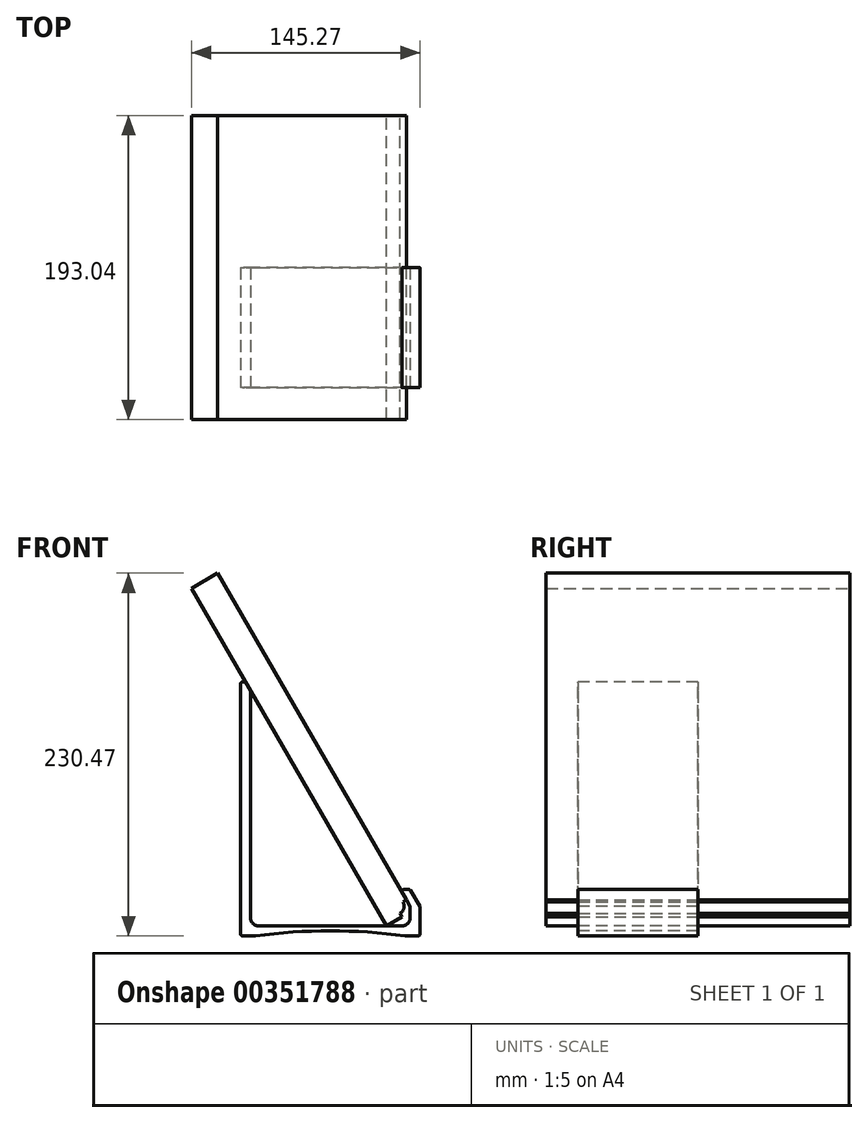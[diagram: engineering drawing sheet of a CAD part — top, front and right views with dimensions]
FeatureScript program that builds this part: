
annotation { "Feature Type Name" : "Feature", "Feature Type Description" : "" }
export const myFeature = defineFeature(function(context is Context, id is Id, definition is map)
    precondition{}
    {
        {
            var Q0;
            Q0=qCreatedBy(makeId("Front.planeOp"),FACE);
            var sketch = newSketch(context, id + "F0", { "sketchPlane" : qUnion([Q0])});
            skLineSegment(sketch, "E0", {"start": v(0, 0) * mm, "end": v(0, 247.65) * mm});
            skLineSegment(sketch, "E1", {"start": v(0, 247.65) * mm, "end": v(19.3, 247.65) * mm});
            skLineSegment(sketch, "E2", {"start": v(19.3, 247.65) * mm, "end": v(19.3, 7.87) * mm});
            skLineSegment(sketch, "E3", {"start": v(19.3, 7.87) * mm, "end": v(16.76, 7.87) * mm});
            skLineSegment(sketch, "E4", {"start": v(11.43, 2.54) * mm, "end": v(11.43, 0) * mm});
            skLineSegment(sketch, "E5", {"start": v(11.43, 0) * mm, "end": v(0, 0) * mm});
            skArc(sketch, "E6", {"start": v(11.43, 2.54) * mm, "mid": v(15.2, 4.1) * mm, "end": v(16.76, 7.87) * mm});
            skSolve(sketch);
        }
        {
            var Q0;
            Q0 = qSketchRegion(id + "F0", true);
            extrude(context, id + "F1", {"entities" : qUnion([Q0]), "endBound" : BoundingType.SYMMETRIC, "depth" : 193.04 * mm});
        }
        {
            var Q0;
            Q0=makeQuery(id+"F1.opExtrude","SWEPT_BODY",BODY,{"disambiguationData":[OSD([sQuery(id+"F0.wireOp",EDGE,"E0"),sQuery(id+"F0.wireOp",EDGE,"E1"),sQuery(id+"F0.wireOp",EDGE,"E2"),sQuery(id+"F0.wireOp",EDGE,"E3"),sQuery(id+"F0.wireOp",EDGE,"E4"),sQuery(id+"F0.wireOp",EDGE,"E5"),sQuery(id+"F0.wireOp",EDGE,"E6")])]});
            var Q1;
            Q1=makeQuery(id+"F1.opExtrude","SWEPT_EDGE",EDGE,{"disambiguationData":[OSD([sQuery(id+"F0.wireOp",EDGE,"E0"),sQuery(id+"F0.wireOp",EDGE,"E5")])]});
            transform(context, id + "F2", {"entities" : qUnion([Q0]), "transformType" : TransformType.ROTATION, "transformAxis" : qUnion([Q1]), "angle" : 30 * degree, "oppositeDirection" : true, "makeCopy" : false});
        }
        {
            var Q0;
            Q0=qCreatedBy(makeId("Front.planeOp"),FACE);
            cPlane(context, id + "F3", {"entities" : qUnion([Q0]), "cplaneType" : CPlaneType.OFFSET, "offset" : 76.2 * mm, "width" : 152.4 * mm, "height" : 152.4 * mm});
        }
        {
            var Q0;
            Q0=qCreatedBy(id+"F3.planeOp",FACE);
            var sketch = newSketch(context, id + "F4", { "sketchPlane" : qUnion([Q0])});
            skLineSegment(sketch, "E7", {"start": v(15.07, 23.07) * mm, "end": v(21.44, 12.03) * mm});
            skLineSegment(sketch, "E8", {"start": v(21.44, 12.03) * mm, "end": v(21.44, -6.35) * mm});
            skLineSegment(sketch, "E9", {"start": v(21.44, -6.35) * mm, "end": v(11.92, -6.35) * mm});
            skLineSegment(sketch, "E10", {"start": v(-92.66, -6.35) * mm, "end": v(-92.66, 155) * mm});
            skLineSegment(sketch, "E11", {"start": v(-92.66, 155) * mm, "end": v(-89.49, 155) * mm});
            skLineSegment(sketch, "E12", {"start": v(-86.31, 149.5) * mm, "end": v(-86.31, 0) * mm});
            skLineSegment(sketch, "E13", {"start": v(-86.31, 0) * mm, "end": v(15.1, 0) * mm});
            skLineSegment(sketch, "E14", {"start": v(15.1, 0) * mm, "end": v(15.1, 12.47) * mm});
            skLineSegment(sketch, "E15", {"start": v(15.1, 12.47) * mm, "end": v(8.97, 23.07) * mm});
            skLineSegment(sketch, "E16", {"start": v(8.97, 23.07) * mm, "end": v(15.07, 23.07) * mm});
            skLineSegment(sketch, "E17", {"start": v(-89.49, 155) * mm, "end": v(-86.31, 149.5) * mm});
            skLineSegment(sketch, "E18", {"start": v(-86.31, 0) * mm, "end": v(-92.66, 0) * mm, "construction": true});
            skLineSegment(sketch, "E19", {"start": v(-86.31, 0) * mm, "end": v(-86.31, -6.35) * mm, "construction": true});
            skLineSegment(sketch, "E20", {"start": v(15.1, 0) * mm, "end": v(21.44, 0) * mm, "construction": true});
            skArc(sketch, "E21", {"start": v(11.92, -6.35) * mm, "mid": v(-35.61, -3.17) * mm, "end": v(-83.14, -6.35) * mm});
            skLineSegment(sketch, "E22.trimOffspring", {"start": v(-83.14, -6.35) * mm, "end": v(-92.66, -6.35) * mm});
            skSolve(sketch);
        }
        {
            var Q0;
            Q0=makeQuery(id+"F4.imprint","IMPRINT",FACE,{"disambiguationData":[TD([[makeQuery(id+"F4.imprint","IMPRINT",EDGE,{"derivedFrom":sQuery(id+"F4.wireOp",EDGE,"E7")}),-1.0]])]});
            extrude(context, id + "F5", {"entities" : qUnion([Q0]), "oppositeDirection" : true, "depth" : 76.2 * mm});
        }
        {
            var Q0;
            Q0=qCreatedBy(makeId("Top.planeOp"),FACE);
            var sketch = newSketch(context, id + "F6", { "sketchPlane" : qUnion([Q0])});
            skLineSegment(sketch, "E23", {"start": v(-35.61, 71.32) * mm, "end": v(-76.79, 0) * mm});
            skLineSegment(sketch, "E24", {"start": v(-76.79, 0) * mm, "end": v(-35.61, -71.32) * mm});
            skLineSegment(sketch, "E25", {"start": v(-35.61, -71.32) * mm, "end": v(5.57, 0) * mm});
            skLineSegment(sketch, "E26", {"start": v(5.57, 0) * mm, "end": v(-35.61, 71.32) * mm});
            skSolve(sketch);
        }
        {
            var Q0;
            Q0=qCreatedBy(makeId("Right.planeOp"),FACE);
            var sketch = newSketch(context, id + "F7", { "sketchPlane" : qUnion([Q0])});
            skLineSegment(sketch, "E27", {"start": v(69.85, 45.1) * mm, "end": v(0, 12.7) * mm});
            skLineSegment(sketch, "E28", {"start": v(0, 12.7) * mm, "end": v(-69.85, 45.1) * mm});
            skLineSegment(sketch, "E29", {"start": v(-69.85, 45.1) * mm, "end": v(0, 77.5) * mm});
            skLineSegment(sketch, "E30", {"start": v(0, 77.5) * mm, "end": v(69.85, 45.1) * mm});
            skLineSegment(sketch, "E31", {"start": v(69.85, 116.25) * mm, "end": v(0, 83.85) * mm});
            skLineSegment(sketch, "E32", {"start": v(0, 83.85) * mm, "end": v(-69.85, 116.25) * mm});
            skLineSegment(sketch, "E33", {"start": v(-69.85, 116.25) * mm, "end": v(0, 148.65) * mm});
            skLineSegment(sketch, "E34", {"start": v(0, 148.65) * mm, "end": v(69.85, 116.25) * mm});
            skLineSegment(sketch, "E35", {"start": v(0, 12.7) * mm, "end": v(0, 77.5) * mm, "construction": true});
            skLineSegment(sketch, "E36", {"start": v(0, 83.85) * mm, "end": v(0, 148.65) * mm, "construction": true});
            skSolve(sketch);
        }
        {
            var Q0;
            Q0=makeQuery(id+"F5.opExtrude","SWEPT_EDGE",EDGE,{"disambiguationData":[OSD([sQuery(id+"F4.wireOp",EDGE,"E15"),sQuery(id+"F4.wireOp",EDGE,"E16")])]});
            var Q1;
            Q1=makeQuery(id+"F5.opExtrude","SWEPT_EDGE",EDGE,{"disambiguationData":[OSD([sQuery(id+"F4.wireOp",EDGE,"E7"),sQuery(id+"F4.wireOp",EDGE,"E16")])]});
            var Q2;
            Q2=makeQuery(id+"F5.opExtrude","SWEPT_EDGE",EDGE,{"disambiguationData":[OSD([sQuery(id+"F4.wireOp",EDGE,"E7"),sQuery(id+"F4.wireOp",EDGE,"E8")])]});
            var Q3;
            Q3=makeQuery(id+"F5.opExtrude","SWEPT_EDGE",EDGE,{"disambiguationData":[OSD([sQuery(id+"F4.wireOp",EDGE,"E8"),sQuery(id+"F4.wireOp",EDGE,"E9")])]});
            var Q4;
            Q4=makeQuery(id+"F5.opExtrude","SWEPT_EDGE",EDGE,{"disambiguationData":[OSD([sQuery(id+"F4.wireOp",EDGE,"E9"),sQuery(id+"F4.wireOp",EDGE,"E21")])]});
            var Q5;
            Q5=makeQuery(id+"F5.opExtrude","SWEPT_EDGE",EDGE,{"disambiguationData":[OSD([sQuery(id+"F4.wireOp",EDGE,"E21"),sQuery(id+"F4.wireOp",EDGE,"E22.trimOffspring")])]});
            var Q6;
            Q6=makeQuery(id+"F5.opExtrude","SWEPT_EDGE",EDGE,{"disambiguationData":[OSD([sQuery(id+"F4.wireOp",EDGE,"E10"),sQuery(id+"F4.wireOp",EDGE,"E22.trimOffspring")])]});
            var Q7;
            Q7=makeQuery(id+"F5.opExtrude","SWEPT_EDGE",EDGE,{"disambiguationData":[OSD([sQuery(id+"F4.wireOp",EDGE,"E10"),sQuery(id+"F4.wireOp",EDGE,"E11")])]});
            var Q8;
            Q8=makeQuery(id+"F5.opExtrude","SWEPT_EDGE",EDGE,{"disambiguationData":[OSD([sQuery(id+"F4.wireOp",EDGE,"E11"),sQuery(id+"F4.wireOp",EDGE,"E17")])]});
            var Q9;
            Q9=makeQuery(id+"F5.opExtrude","SWEPT_EDGE",EDGE,{"disambiguationData":[OSD([sQuery(id+"F4.wireOp",EDGE,"E12"),sQuery(id+"F4.wireOp",EDGE,"E17")])]});
            fillet(context, id + "F8", {"entities" : qUnion([Q0, Q1, Q2, Q3, Q4, Q5, Q6, Q7, Q8, Q9]), "radius" : 1.27 * mm, "tangentPropagation" : true, "allowEdgeOverflow" : false});
        }
        {
            var Q0;
            Q0=makeQuery(id+"F5.opExtrude","SWEPT_EDGE",EDGE,{"disambiguationData":[OSD([sQuery(id+"F4.wireOp",EDGE,"E12"),sQuery(id+"F4.wireOp",EDGE,"E13")])]});
            var Q1;
            Q1=makeQuery(id+"F5.opExtrude","SWEPT_EDGE",EDGE,{"disambiguationData":[OSD([sQuery(id+"F4.wireOp",EDGE,"E13"),sQuery(id+"F4.wireOp",EDGE,"E14")])]});
            fillet(context, id + "F9", {"entities" : qUnion([Q0, Q1]), "radius" : 5.08 * mm, "tangentPropagation" : true, "allowEdgeOverflow" : false});
        }
    });
